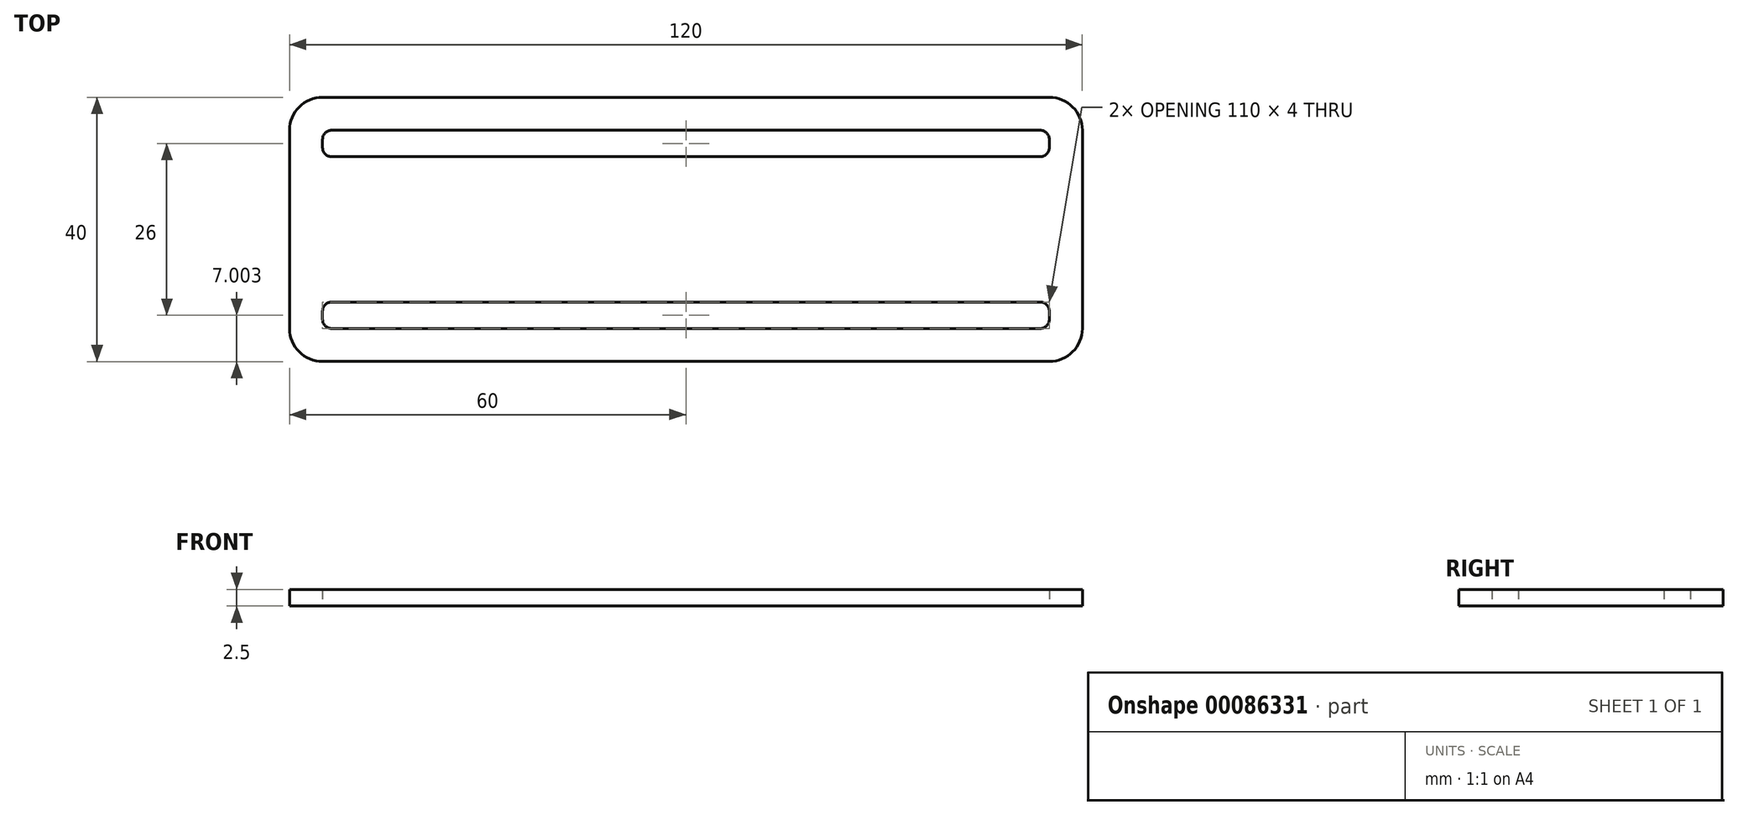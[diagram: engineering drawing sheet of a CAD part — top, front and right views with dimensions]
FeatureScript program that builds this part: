
annotation { "Feature Type Name" : "Feature", "Feature Type Description" : "" }
export const myFeature = defineFeature(function(context is Context, id is Id, definition is map)
    precondition{}
    {
        {
            var Q0;
            Q0=qCreatedBy(makeId("Top.planeOp"),FACE);
            var sketch = newSketch(context, id + "F0", { "sketchPlane" : qUnion([Q0])});
            skLineSegment(sketch, "E0.bottom", {"start": v(-58.09, 20.64) * mm, "end": v(51.91, 20.64) * mm});
            skLineSegment(sketch, "E0.top", {"start": v(-58.09, -19.36) * mm, "end": v(51.91, -19.36) * mm});
            skLineSegment(sketch, "E0.left", {"start": v(-63.09, 15.64) * mm, "end": v(-63.09, -14.36) * mm});
            skLineSegment(sketch, "E0.right", {"start": v(56.91, 15.64) * mm, "end": v(56.91, -14.36) * mm});
            skPoint(sketch, "E1.visualSharp", {"position": v(-63.09, 20.64) * mm});
            skArc(sketch, "E1.filletArc", {"start": v(-58.09, 20.64) * mm, "mid": v(-61.63, 19.18) * mm, "end": v(-63.09, 15.64) * mm});
            skPoint(sketch, "E2.visualSharp", {"position": v(56.91, 20.64) * mm});
            skArc(sketch, "E2.filletArc", {"start": v(56.91, 15.64) * mm, "mid": v(55.45, 19.18) * mm, "end": v(51.91, 20.64) * mm});
            skPoint(sketch, "E3.visualSharp", {"position": v(56.91, -19.36) * mm});
            skArc(sketch, "E3.filletArc", {"start": v(51.91, -19.36) * mm, "mid": v(55.45, -17.9) * mm, "end": v(56.91, -14.36) * mm});
            skPoint(sketch, "E4.visualSharp", {"position": v(-63.09, -19.36) * mm});
            skArc(sketch, "E4.filletArc", {"start": v(-63.09, -14.36) * mm, "mid": v(-61.63, -17.9) * mm, "end": v(-58.09, -19.36) * mm});
            skLineSegment(sketch, "E5.bottom", {"start": v(-56.72, 15.64) * mm, "end": v(50.54, 15.64) * mm});
            skLineSegment(sketch, "E5.top", {"start": v(-56.72, 11.64) * mm, "end": v(50.54, 11.64) * mm});
            skLineSegment(sketch, "E5.left", {"start": v(-58.09, 14.27) * mm, "end": v(-58.09, 13.01) * mm});
            skLineSegment(sketch, "E5.right", {"start": v(51.91, 14.27) * mm, "end": v(51.91, 13.01) * mm});
            skArc(sketch, "E6.filletArc", {"start": v(-56.72, 15.64) * mm, "mid": v(-57.69, 15.24) * mm, "end": v(-58.09, 14.27) * mm});
            skArc(sketch, "E7.filletArc", {"start": v(51.91, 14.27) * mm, "mid": v(51.5, 15.24) * mm, "end": v(50.54, 15.64) * mm});
            skPoint(sketch, "E8.visualSharp", {"position": v(51.91, 11.64) * mm});
            skArc(sketch, "E8.filletArc", {"start": v(50.54, 11.64) * mm, "mid": v(51.5, 12.04) * mm, "end": v(51.91, 13.01) * mm});
            skPoint(sketch, "E9.visualSharp", {"position": v(-58.09, 11.64) * mm});
            skArc(sketch, "E9.filletArc", {"start": v(-58.09, 13.01) * mm, "mid": v(-57.69, 12.04) * mm, "end": v(-56.72, 11.64) * mm});
            skLineSegment(sketch, "E10.bottom", {"start": v(-56.72, -14.36) * mm, "end": v(50.54, -14.36) * mm});
            skLineSegment(sketch, "E10.top", {"start": v(-56.72, -10.36) * mm, "end": v(50.54, -10.36) * mm});
            skLineSegment(sketch, "E10.left", {"start": v(-58.09, -12.99) * mm, "end": v(-58.09, -11.73) * mm});
            skLineSegment(sketch, "E10.right", {"start": v(51.91, -12.99) * mm, "end": v(51.91, -11.73) * mm});
            skPoint(sketch, "E11.visualSharp", {"position": v(-58.09, -10.36) * mm});
            skArc(sketch, "E11.filletArc", {"start": v(-56.72, -10.36) * mm, "mid": v(-57.69, -10.76) * mm, "end": v(-58.09, -11.73) * mm});
            skPoint(sketch, "E12.visualSharp", {"position": v(51.91, -10.36) * mm});
            skArc(sketch, "E12.filletArc", {"start": v(51.91, -11.73) * mm, "mid": v(51.5, -10.76) * mm, "end": v(50.54, -10.36) * mm});
            skArc(sketch, "E13.filletArc", {"start": v(50.54, -14.36) * mm, "mid": v(51.5, -13.96) * mm, "end": v(51.91, -12.99) * mm});
            skArc(sketch, "E14.filletArc", {"start": v(-58.09, -12.99) * mm, "mid": v(-57.69, -13.96) * mm, "end": v(-56.72, -14.36) * mm});
            skSolve(sketch);
        }
        {
            var Q0;
            Q0=makeQuery(id+"F0.imprint","IMPRINT",FACE,{"disambiguationData":[TD([[makeQuery(id+"F0.imprint","IMPRINT",EDGE,{"derivedFrom":sQuery(id+"F0.wireOp",EDGE,"E0.bottom")}),-1.0]])]});
            extrude(context, id + "F1", {"entities" : qUnion([Q0]), "depth" : 2.5 * mm});
        }
    });
